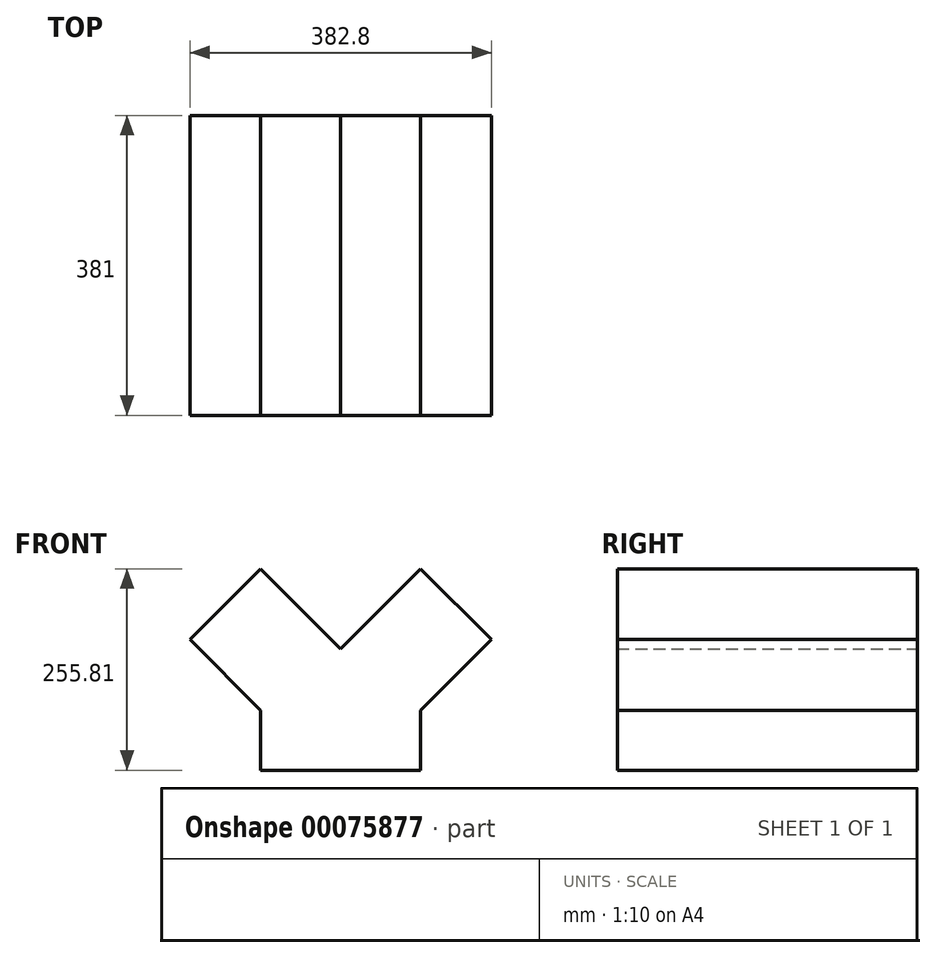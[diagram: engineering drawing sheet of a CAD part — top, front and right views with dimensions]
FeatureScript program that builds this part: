
annotation { "Feature Type Name" : "Feature", "Feature Type Description" : "" }
export const myFeature = defineFeature(function(context is Context, id is Id, definition is map)
    precondition{}
    {
        {
            var Q0;
            Q0=qCreatedBy(makeId("Front.planeOp"),FACE);
            var sketch = newSketch(context, id + "F0", { "sketchPlane" : qUnion([Q0])});
            skLineSegment(sketch, "E0", {"start": v(-101.6, -76.2) * mm, "end": v(101.6, -76.2) * mm});
            skLineSegment(sketch, "E1", {"start": v(101.6, -76.2) * mm, "end": v(101.6, 0) * mm});
            skLineSegment(sketch, "E2", {"start": v(101.6, 0) * mm, "end": v(191.4, 89.8) * mm});
            skLineSegment(sketch, "E3", {"start": v(191.4, 89.8) * mm, "end": v(101.6, 179.6) * mm});
            skLineSegment(sketch, "E4", {"start": v(101.6, 179.6) * mm, "end": v(0, 78) * mm});
            skLineSegment(sketch, "E5", {"start": v(0, 78) * mm, "end": v(-101.6, 179.6) * mm});
            skLineSegment(sketch, "E6", {"start": v(-101.6, 179.6) * mm, "end": v(-191.4, 89.8) * mm});
            skLineSegment(sketch, "E7", {"start": v(-191.4, 89.8) * mm, "end": v(-101.6, 0) * mm});
            skLineSegment(sketch, "E8", {"start": v(-101.6, 0) * mm, "end": v(-101.6, -76.2) * mm});
            skSolve(sketch);
        }
        {
            var Q0;
            Q0 = qSketchRegion(id + "F0", true);
            extrude(context, id + "F1", {"entities" : qUnion([Q0]), "endBound" : BoundingType.SYMMETRIC, "depth" : 381 * mm});
        }
    });
